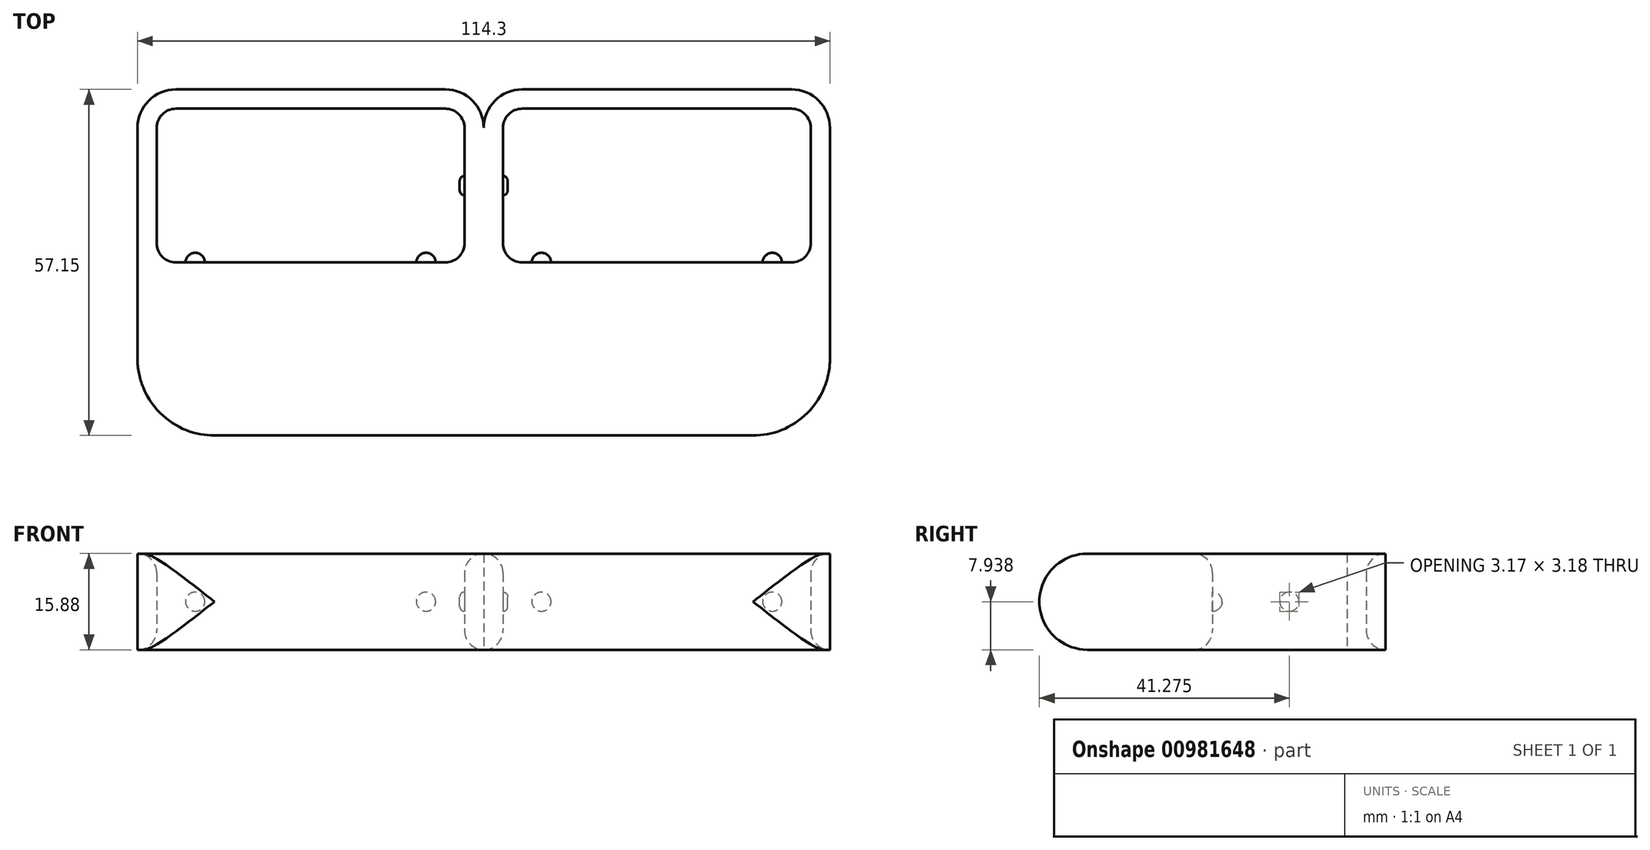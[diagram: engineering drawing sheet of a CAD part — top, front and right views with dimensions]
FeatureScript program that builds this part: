
annotation { "Feature Type Name" : "Feature", "Feature Type Description" : "" }
export const myFeature = defineFeature(function(context is Context, id is Id, definition is map)
    precondition{}
    {
        {
            var Q0;
            Q0=qCreatedBy(makeId("Top.planeOp"),FACE);
            var sketch = newSketch(context, id + "F0", { "sketchPlane" : qUnion([Q0])});
            skLineSegment(sketch, "E0.bottom", {"start": v(-6.35, 0) * mm, "end": v(-15.88, 0) * mm});
            skLineSegment(sketch, "E0.top", {"start": v(-6.35, 31.75) * mm, "end": v(-50.8, 31.75) * mm});
            skLineSegment(sketch, "E0.left", {"start": v(0, 6.35) * mm, "end": v(0, 25.4) * mm});
            skLineSegment(sketch, "E0.right", {"start": v(-57.15, 6.35) * mm, "end": v(-57.15, 25.4) * mm});
            skPoint(sketch, "E0.middle", {"position": v(-28.58, 15.88) * mm});
            skLineSegment(sketch, "E1.bottom", {"start": v(6.35, 0) * mm, "end": v(15.88, 0) * mm});
            skLineSegment(sketch, "E1.top", {"start": v(6.35, 31.75) * mm, "end": v(50.8, 31.75) * mm});
            skLineSegment(sketch, "E1.left", {"start": v(0, 6.35) * mm, "end": v(0, 31.75) * mm});
            skLineSegment(sketch, "E1.right", {"start": v(57.15, 6.35) * mm, "end": v(57.15, 25.4) * mm});
            skPoint(sketch, "E1.middle", {"position": v(28.58, 15.87) * mm});
            skLineSegment(sketch, "E2.bottom", {"start": v(50.8, 3.17) * mm, "end": v(41.28, 3.17) * mm});
            skLineSegment(sketch, "E2.top", {"start": v(50.8, 28.57) * mm, "end": v(6.35, 28.57) * mm});
            skLineSegment(sketch, "E2.left", {"start": v(53.98, 6.35) * mm, "end": v(53.98, 25.4) * mm});
            skLineSegment(sketch, "E2.right", {"start": v(3.18, 6.35) * mm, "end": v(3.18, 25.4) * mm});
            skLineSegment(sketch, "E3.bottom", {"start": v(-6.35, 3.17) * mm, "end": v(-15.88, 3.17) * mm});
            skLineSegment(sketch, "E3.top", {"start": v(-6.35, 28.57) * mm, "end": v(-50.8, 28.57) * mm});
            skLineSegment(sketch, "E3.left", {"start": v(-3.18, 6.35) * mm, "end": v(-3.18, 25.4) * mm});
            skLineSegment(sketch, "E3.right", {"start": v(-53.98, 6.35) * mm, "end": v(-53.98, 25.4) * mm});
            skLineSegment(sketch, "E4", {"start": v(15.88, 3.17) * mm, "end": v(15.88, 0) * mm});
            skLineSegment(sketch, "E5", {"start": v(41.28, 3.17) * mm, "end": v(41.28, 0) * mm});
            skLineSegment(sketch, "E6.trimOffspring", {"start": v(15.88, 3.17) * mm, "end": v(6.35, 3.17) * mm});
            skLineSegment(sketch, "E7.trimOffspring", {"start": v(41.28, 0) * mm, "end": v(50.8, 0) * mm});
            skLineSegment(sketch, "E8.MirrorCS", {"start": v(-15.88, 3.17) * mm, "end": v(-15.88, 0) * mm});
            skLineSegment(sketch, "E9.MirrorCS", {"start": v(-41.28, 3.17) * mm, "end": v(-41.28, 0) * mm});
            skLineSegment(sketch, "E10.trimOffspring", {"start": v(-41.28, 3.17) * mm, "end": v(-50.8, 3.17) * mm});
            skLineSegment(sketch, "E11.trimOffspring", {"start": v(-41.28, 0) * mm, "end": v(-50.8, 0) * mm});
            skPoint(sketch, "E12.visualSharp", {"position": v(-3.18, 3.17) * mm});
            skArc(sketch, "E12.filletArc", {"start": v(-6.35, 3.17) * mm, "mid": v(-4.1, 4.1) * mm, "end": v(-3.18, 6.35) * mm});
            skPoint(sketch, "E13.visualSharp", {"position": v(-3.18, 28.57) * mm});
            skArc(sketch, "E13.filletArc", {"start": v(-3.18, 25.4) * mm, "mid": v(-4.1, 27.65) * mm, "end": v(-6.35, 28.57) * mm});
            skPoint(sketch, "E14.visualSharp", {"position": v(-53.98, 28.57) * mm});
            skArc(sketch, "E14.filletArc", {"start": v(-50.8, 28.57) * mm, "mid": v(-53.05, 27.65) * mm, "end": v(-53.98, 25.4) * mm});
            skPoint(sketch, "E15.visualSharp", {"position": v(-53.98, 3.17) * mm});
            skArc(sketch, "E15.filletArc", {"start": v(-53.98, 6.35) * mm, "mid": v(-53.05, 4.1) * mm, "end": v(-50.8, 3.17) * mm});
            skPoint(sketch, "E16.visualSharp", {"position": v(3.18, 28.57) * mm});
            skArc(sketch, "E16.filletArc", {"start": v(6.35, 28.57) * mm, "mid": v(4.1, 27.65) * mm, "end": v(3.18, 25.4) * mm});
            skPoint(sketch, "E17.visualSharp", {"position": v(3.18, 3.17) * mm});
            skArc(sketch, "E17.filletArc", {"start": v(3.18, 6.35) * mm, "mid": v(4.1, 4.1) * mm, "end": v(6.35, 3.17) * mm});
            skPoint(sketch, "E18.visualSharp", {"position": v(53.98, 28.57) * mm});
            skArc(sketch, "E18.filletArc", {"start": v(53.98, 25.4) * mm, "mid": v(53.05, 27.65) * mm, "end": v(50.8, 28.57) * mm});
            skPoint(sketch, "E19.visualSharp", {"position": v(53.98, 3.17) * mm});
            skArc(sketch, "E19.filletArc", {"start": v(50.8, 3.17) * mm, "mid": v(53.05, 4.1) * mm, "end": v(53.98, 6.35) * mm});
            skPoint(sketch, "E20.visualSharp", {"position": v(57.15, 0) * mm});
            skArc(sketch, "E20.filletArc", {"start": v(50.8, 0) * mm, "mid": v(55.3, 1.86) * mm, "end": v(57.15, 6.35) * mm});
            skPoint(sketch, "E21.visualSharp", {"position": v(57.15, 31.75) * mm});
            skArc(sketch, "E21.filletArc", {"start": v(57.15, 25.4) * mm, "mid": v(55.3, 29.9) * mm, "end": v(50.8, 31.75) * mm});
            skPoint(sketch, "E22.visualSharp", {"position": v(0, 31.75) * mm});
            skArc(sketch, "E22.filletArc", {"start": v(6.35, 31.75) * mm, "mid": v(1.86, 29.9) * mm, "end": v(0, 25.4) * mm});
            skArc(sketch, "E23.filletArc", {"start": v(0, 25.4) * mm, "mid": v(-1.86, 29.9) * mm, "end": v(-6.35, 31.75) * mm});
            skPoint(sketch, "E24.visualSharp", {"position": v(0, 0) * mm});
            skArc(sketch, "E24.filletArc", {"start": v(-6.35, 0) * mm, "mid": v(-1.86, 1.86) * mm, "end": v(0, 6.35) * mm});
            skArc(sketch, "E25.filletArc", {"start": v(0, 6.35) * mm, "mid": v(1.86, 1.86) * mm, "end": v(6.35, 0) * mm});
            skPoint(sketch, "E26.visualSharp", {"position": v(-57.15, 31.75) * mm});
            skArc(sketch, "E26.filletArc", {"start": v(-50.8, 31.75) * mm, "mid": v(-55.3, 29.9) * mm, "end": v(-57.15, 25.4) * mm});
            skPoint(sketch, "E27.visualSharp", {"position": v(-57.15, 0) * mm});
            skArc(sketch, "E27.filletArc", {"start": v(-57.15, 6.35) * mm, "mid": v(-55.3, 1.86) * mm, "end": v(-50.8, 0) * mm});
            skSolve(sketch);
        }
        {
            var Q0;
            Q0 = qSketchRegion(id + "F0", true);
            extrude(context, id + "F1", {"entities" : qUnion([Q0]), "depth" : 15.88 * mm, "offsetDistance" : 25.4 * mm});
        }
        {
            var Q0;
            Q0=qCreatedBy(makeId("Top.planeOp"),FACE);
            var sketch = newSketch(context, id + "F2", { "sketchPlane" : qUnion([Q0])});
            skLineSegment(sketch, "E28.bottom", {"start": v(50.8, 0) * mm, "end": v(41.28, 0) * mm});
            skLineSegment(sketch, "E28.top", {"start": v(44.45, -25.4) * mm, "end": v(-44.45, -25.4) * mm});
            skLineSegment(sketch, "E28.left", {"start": v(57.15, 0) * mm, "end": v(57.15, -12.7) * mm});
            skLineSegment(sketch, "E28.right", {"start": v(-57.15, 0) * mm, "end": v(-57.15, -12.7) * mm});
            skPoint(sketch, "E28.middle", {"position": v(0, -12.7) * mm});
            skLineSegment(sketch, "E29", {"start": v(57.15, 0) * mm, "end": v(57.15, 6.35) * mm});
            skArc(sketch, "E30", {"start": v(50.8, 0) * mm, "mid": v(55.3, 1.86) * mm, "end": v(57.15, 6.35) * mm});
            skLineSegment(sketch, "E31", {"start": v(0, 0) * mm, "end": v(0, -25.4) * mm, "construction": true});
            skPoint(sketch, "E32.visualSharp", {"position": v(57.15, -25.4) * mm});
            skArc(sketch, "E32.filletArc", {"start": v(44.45, -25.4) * mm, "mid": v(53.43, -21.68) * mm, "end": v(57.15, -12.7) * mm});
            skArc(sketch, "E33.MirrorCS", {"start": v(-44.45, -25.4) * mm, "mid": v(-53.43, -21.68) * mm, "end": v(-57.15, -12.7) * mm});
            skLineSegment(sketch, "E34.MirrorCS", {"start": v(-57.15, 0) * mm, "end": v(-57.15, 6.35) * mm});
            skArc(sketch, "E35.MirrorCS", {"start": v(-50.8, 0) * mm, "mid": v(-55.3, 1.86) * mm, "end": v(-57.15, 6.35) * mm});
            skPoint(sketch, "E36.orphan", {"position": v(-57.15, -25.4) * mm});
            skLineSegment(sketch, "E37.top", {"start": v(-41.28, 3.17) * mm, "end": v(-15.88, 3.17) * mm});
            skLineSegment(sketch, "E37.left", {"start": v(-41.28, 0) * mm, "end": v(-41.28, 3.17) * mm});
            skLineSegment(sketch, "E37.right", {"start": v(-15.88, 0) * mm, "end": v(-15.88, 3.17) * mm});
            skLineSegment(sketch, "E38.top", {"start": v(15.88, 3.17) * mm, "end": v(41.28, 3.17) * mm});
            skLineSegment(sketch, "E38.left", {"start": v(15.88, 0) * mm, "end": v(15.88, 3.17) * mm});
            skLineSegment(sketch, "E38.right", {"start": v(41.28, 0) * mm, "end": v(41.28, 3.17) * mm});
            skLineSegment(sketch, "E39.trimOffspring", {"start": v(-41.28, 0) * mm, "end": v(-50.8, 0) * mm});
            skLineSegment(sketch, "E40.trimOffspring", {"start": v(15.88, 0) * mm, "end": v(6.35, 0) * mm});
            skArc(sketch, "E41", {"start": v(0, 6.35) * mm, "mid": v(1.86, 1.86) * mm, "end": v(6.35, 0) * mm});
            skArc(sketch, "E42", {"start": v(-6.35, 0) * mm, "mid": v(-1.86, 1.86) * mm, "end": v(0, 6.35) * mm});
            skLineSegment(sketch, "E43.trimOffspring", {"start": v(-6.35, 0) * mm, "end": v(-15.88, 0) * mm});
            skSolve(sketch);
        }
        {
            var Q0;
            Q0=makeQuery(id+"F2.imprint","IMPRINT",FACE,{"disambiguationData":[TD([[makeQuery(id+"F2.imprint","IMPRINT",EDGE,{"derivedFrom":sQuery(id+"F2.wireOp",EDGE,"E28.bottom")}),1.0]])]});
            extrude(context, id + "F3", {"entities" : qUnion([Q0]), "depth" : 15.88 * mm, "offsetDistance" : 25.4 * mm});
        }
        {
            var Q0;
            Q0=qCreatedBy(makeId("Right.planeOp"),FACE);
            var sketch = newSketch(context, id + "F4", { "sketchPlane" : qUnion([Q0])});
            skCircle(sketch, "E44", {"center": v(15.88, 7.94) * mm, "radius": 1.59 * mm});
            skSolve(sketch);
        }
        {
            var Q0;
            Q0 = qSketchRegion(id + "F4", true);
            extrude(context, id + "F5", {"entities" : qUnion([Q0]), "operationType" : NewBodyOperationType.ADD, "depth" : 3.97 * mm, "offsetDistance" : 25.4 * mm, "hasSecondDirection" : true, "secondDirectionOppositeDirection" : true, "secondDirectionDepth" : 3.97 * mm});
        }
        {
            var Q0;
            Q0=makeQuery(id+"F5.opExtrude","CAP_EDGE",EDGE,{"disambiguationData":[OSD([sQuery(id+"F4.wireOp",EDGE,"E44")])],"isStart":true});
            var Q1;
            Q1=makeQuery(id+"F5.opExtrude","CAP_EDGE",EDGE,{"disambiguationData":[OSD([sQuery(id+"F4.wireOp",EDGE,"E44")])],"isStart":false});
            fillet(context, id + "F6", {"entities" : qUnion([Q0, Q1]), "radius" : 0.8 * mm, "tangentPropagation" : true, "allowEdgeOverflow" : false});
        }
        {
            var Q0;
            Q0=qCreatedBy(makeId("Front.planeOp"),FACE);
            var sketch = newSketch(context, id + "F7", { "sketchPlane" : qUnion([Q0])});
            skCircle(sketch, "E45", {"center": v(-9.52, 7.94) * mm, "radius": 1.59 * mm});
            skCircle(sketch, "E46", {"center": v(9.53, 7.94) * mm, "radius": 1.59 * mm});
            skCircle(sketch, "E47", {"center": v(-47.62, 7.94) * mm, "radius": 1.59 * mm});
            skCircle(sketch, "E48", {"center": v(47.62, 7.94) * mm, "radius": 1.59 * mm});
            skSolve(sketch);
        }
        {
            var Q0;
            Q0 = qSketchRegion(id + "F7", true);
            extrude(context, id + "F8", {"entities" : qUnion([Q0]), "operationType" : NewBodyOperationType.ADD, "depth" : 22.22 * mm, "offsetDistance" : 25.4 * mm, "hasSecondDirection" : true, "secondDirectionOppositeDirection" : true, "secondDirectionDepth" : 4.76 * mm});
        }
        {
            var Q0;
            Q0=makeQuery(id+"F8.opExtrude","CAP_EDGE",EDGE,{"disambiguationData":[OSD([sQuery(id+"F7.wireOp",EDGE,"E48")])],"isStart":true});
            var Q1;
            Q1=makeQuery(id+"F8.opExtrude","CAP_EDGE",EDGE,{"disambiguationData":[OSD([sQuery(id+"F7.wireOp",EDGE,"E46")])],"isStart":true});
            var Q2;
            Q2=makeQuery(id+"F8.opExtrude","CAP_EDGE",EDGE,{"disambiguationData":[OSD([sQuery(id+"F7.wireOp",EDGE,"E45")])],"isStart":true});
            var Q3;
            Q3=makeQuery(id+"F8.opExtrude","CAP_EDGE",EDGE,{"disambiguationData":[OSD([sQuery(id+"F7.wireOp",EDGE,"E47")])],"isStart":true});
            fillet(context, id + "F9", {"entities" : qUnion([Q0, Q1, Q2, Q3]), "radius" : 1.59 * mm, "tangentPropagation" : true, "allowEdgeOverflow" : false});
        }
        {
            var Q0;
            Q0=makeQuery(id+"F3.opExtrude","CAP_EDGE",EDGE,{"disambiguationData":[OSD([sQuery(id+"F2.wireOp",EDGE,"E28.top")])],"isStart":false});
            var Q1;
            Q1=makeQuery(id+"F3.opExtrude","CAP_EDGE",EDGE,{"disambiguationData":[OSD([sQuery(id+"F2.wireOp",EDGE,"E28.top")])],"isStart":true});
            fillet(context, id + "F10", {"entities" : qUnion([Q0, Q1]), "radius" : 7.94 * mm, "allowEdgeOverflow" : false});
        }
        {
            var Q0;
            Q0=makeQuery(id+"F3.opExtrude","CAP_EDGE",EDGE,{"disambiguationData":[OSD([sQuery(id+"F2.wireOp",EDGE,"E37.top")])],"isStart":true});
            var Q1;
            Q1=makeQuery(id+"F3.opExtrude","CAP_EDGE",EDGE,{"disambiguationData":[OSD([sQuery(id+"F2.wireOp",EDGE,"E37.top")])],"isStart":false});
            var Q2;
            Q2=makeQuery(id+"F3.opExtrude","CAP_EDGE",EDGE,{"disambiguationData":[OSD([sQuery(id+"F2.wireOp",EDGE,"E38.top")])],"isStart":true});
            var Q3;
            Q3=makeQuery(id+"F3.opExtrude","CAP_EDGE",EDGE,{"disambiguationData":[OSD([sQuery(id+"F2.wireOp",EDGE,"E38.top")])],"isStart":false});
            var Q4;
            Q4=makeQuery(id+"F1.opExtrude","CAP_EDGE",EDGE,{"disambiguationData":[OSD([sQuery(id+"F0.wireOp",EDGE,"E6.trimOffspring")])],"isStart":false});
            var Q5;
            Q5=makeQuery(id+"F1.opExtrude","CAP_EDGE",EDGE,{"disambiguationData":[OSD([sQuery(id+"F0.wireOp",EDGE,"E6.trimOffspring")])],"isStart":true});
            var Q6;
            Q6=makeQuery(id+"F1.opExtrude","CAP_EDGE",EDGE,{"disambiguationData":[OSD([sQuery(id+"F0.wireOp",EDGE,"E2.bottom")])],"isStart":true});
            var Q7;
            Q7=makeQuery(id+"F1.opExtrude","CAP_EDGE",EDGE,{"disambiguationData":[OSD([sQuery(id+"F0.wireOp",EDGE,"E2.bottom")])],"isStart":false});
            var Q8;
            Q8=makeQuery(id+"F1.opExtrude","CAP_EDGE",EDGE,{"disambiguationData":[OSD([sQuery(id+"F0.wireOp",EDGE,"E3.bottom")])],"isStart":true});
            var Q9;
            Q9=makeQuery(id+"F1.opExtrude","CAP_EDGE",EDGE,{"disambiguationData":[OSD([sQuery(id+"F0.wireOp",EDGE,"E3.bottom")])],"isStart":false});
            var Q10;
            Q10=makeQuery(id+"F1.opExtrude","CAP_EDGE",EDGE,{"disambiguationData":[OSD([sQuery(id+"F0.wireOp",EDGE,"E10.trimOffspring")])],"isStart":false});
            var Q11;
            Q11=makeQuery(id+"F1.opExtrude","CAP_EDGE",EDGE,{"disambiguationData":[OSD([sQuery(id+"F0.wireOp",EDGE,"E10.trimOffspring")])],"isStart":true});
            var Q12;
            Q12=makeQuery(id+"F1.opExtrude","CAP_EDGE",EDGE,{"disambiguationData":[OSD([sQuery(id+"F0.wireOp",EDGE,"E12.filletArc")])],"isStart":true});
            var Q13;
            Q13=makeQuery(id+"F1.opExtrude","CAP_EDGE",EDGE,{"disambiguationData":[OSD([sQuery(id+"F0.wireOp",EDGE,"E3.left")])],"isStart":true});
            var Q14;
            Q14=makeQuery(id+"F1.opExtrude","CAP_EDGE",EDGE,{"disambiguationData":[OSD([sQuery(id+"F0.wireOp",EDGE,"E3.left")])],"isStart":false});
            var Q15;
            Q15=makeQuery(id+"F1.opExtrude","CAP_EDGE",EDGE,{"disambiguationData":[OSD([sQuery(id+"F0.wireOp",EDGE,"E12.filletArc")])],"isStart":false});
            var Q16;
            Q16=makeQuery(id+"F1.opExtrude","CAP_EDGE",EDGE,{"disambiguationData":[OSD([sQuery(id+"F0.wireOp",EDGE,"E2.right")])],"isStart":true});
            var Q17;
            Q17=makeQuery(id+"F1.opExtrude","CAP_EDGE",EDGE,{"disambiguationData":[OSD([sQuery(id+"F0.wireOp",EDGE,"E2.right")])],"isStart":false});
            var Q18;
            Q18=makeQuery(id+"F1.opExtrude","CAP_EDGE",EDGE,{"disambiguationData":[OSD([sQuery(id+"F0.wireOp",EDGE,"E17.filletArc")])],"isStart":true});
            var Q19;
            Q19=makeQuery(id+"F1.opExtrude","CAP_EDGE",EDGE,{"disambiguationData":[OSD([sQuery(id+"F0.wireOp",EDGE,"E17.filletArc")])],"isStart":false});
            fillet(context, id + "F11", {"entities" : qUnion([Q0, Q1, Q2, Q3, Q4, Q5, Q6, Q7, Q8, Q9, Q10, Q11, Q12, Q13, Q14, Q15, Q16, Q17, Q18, Q19]), "radius" : 3.17 * mm, "tangentPropagation" : true, "allowEdgeOverflow" : false});
        }
    });
